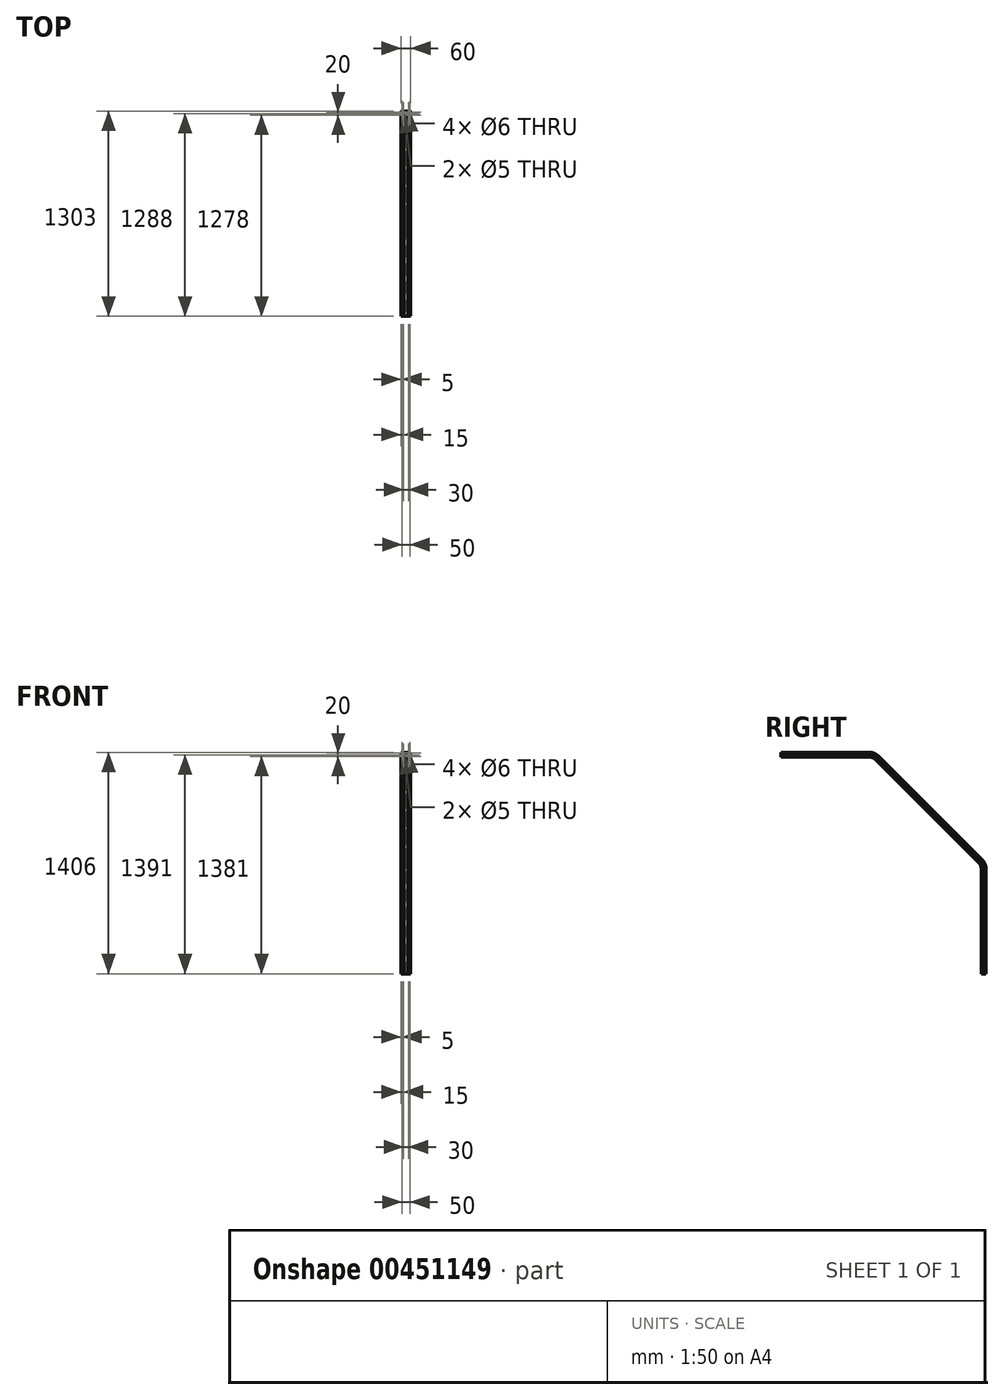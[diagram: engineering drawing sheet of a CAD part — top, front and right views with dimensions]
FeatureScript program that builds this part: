
annotation { "Feature Type Name" : "Feature", "Feature Type Description" : "" }
export const myFeature = defineFeature(function(context is Context, id is Id, definition is map)
    precondition{}
    {
        {
            var Q0;
            Q0=qCreatedBy(makeId("Top.planeOp"),FACE);
            var sketch = newSketch(context, id + "F0", { "sketchPlane" : qUnion([Q0])});
            skLineSegment(sketch, "E0.bottom", {"start": v(30, -15) * mm, "end": v(18.15, -15) * mm});
            skLineSegment(sketch, "E0.top", {"start": v(30, 15) * mm, "end": v(18.15, 15) * mm});
            skLineSegment(sketch, "E0.left", {"start": v(30, -15) * mm, "end": v(30, -3.15) * mm});
            skLineSegment(sketch, "E0.right", {"start": v(-30, -15) * mm, "end": v(-30, -3.15) * mm});
            skPoint(sketch, "E0.middle", {"position": v(0, 0) * mm});
            skLineSegment(sketch, "E1.left", {"start": v(-11.85, 12.5) * mm, "end": v(-11.85, 15) * mm});
            skLineSegment(sketch, "E1.right", {"start": v(-18.15, 12.5) * mm, "end": v(-18.15, 15) * mm});
            skPoint(sketch, "E1.middle", {"position": v(-15, 13.75) * mm});
            skLineSegment(sketch, "E2.bottom", {"start": v(-9.85, 12.5) * mm, "end": v(-11.85, 12.5) * mm});
            skLineSegment(sketch, "E2.left", {"start": v(-9.85, 12.5) * mm, "end": v(-9.85, 6.55) * mm});
            skLineSegment(sketch, "E2.right", {"start": v(-20.15, 12.5) * mm, "end": v(-20.15, 6.55) * mm});
            skPoint(sketch, "E2.middle", {"position": v(-15, 9.52) * mm});
            skArc(sketch, "E3", {"start": v(-20.15, 6.55) * mm, "mid": v(-15, 4.5) * mm, "end": v(-9.85, 6.55) * mm});
            skPoint(sketch, "E4.MirrorP", {"position": v(15, 9.52) * mm});
            skPoint(sketch, "E5.MirrorP", {"position": v(15, 13.75) * mm});
            skLineSegment(sketch, "E6.MirrorCS", {"start": v(11.85, 12.5) * mm, "end": v(11.85, 15) * mm});
            skLineSegment(sketch, "E7.MirrorCS", {"start": v(18.15, 12.5) * mm, "end": v(18.15, 15) * mm});
            skLineSegment(sketch, "E8.MirrorCS", {"start": v(9.85, 12.5) * mm, "end": v(11.85, 12.5) * mm});
            skLineSegment(sketch, "E9.MirrorCS", {"start": v(9.85, 12.5) * mm, "end": v(9.85, 6.55) * mm});
            skArc(sketch, "E10.MirrorCS", {"start": v(20.15, 6.55) * mm, "mid": v(15, 4.5) * mm, "end": v(9.85, 6.55) * mm});
            skLineSegment(sketch, "E11.MirrorCS", {"start": v(20.15, 12.5) * mm, "end": v(20.15, 6.55) * mm});
            skLineSegment(sketch, "E12.trimOffspring", {"start": v(-18.15, 12.5) * mm, "end": v(-20.15, 12.5) * mm});
            skLineSegment(sketch, "E13.trimOffspring", {"start": v(18.15, 12.5) * mm, "end": v(20.15, 12.5) * mm});
            skCircle(sketch, "E14", {"center": v(-15, 0) * mm, "radius": 2.5 * mm});
            skCircle(sketch, "E15", {"center": v(-25, 10) * mm, "radius": 3 * mm});
            skCircle(sketch, "E16.MirrorC", {"center": v(25, 10) * mm, "radius": 3 * mm});
            skCircle(sketch, "E17.MirrorC", {"center": v(25, -10) * mm, "radius": 3 * mm});
            skCircle(sketch, "E18.MirrorC", {"center": v(-25, -10) * mm, "radius": 3 * mm});
            skCircle(sketch, "E19.MirrorC", {"center": v(15, 0) * mm, "radius": 2.5 * mm});
            skLineSegment(sketch, "E20", {"start": v(-7, 12.5) * mm, "end": v(0, 12.5) * mm});
            skLineSegment(sketch, "E21", {"start": v(-7, 12.5) * mm, "end": v(-7, 7) * mm});
            skLineSegment(sketch, "E22", {"start": v(-10, 0) * mm, "end": v(-7, 7) * mm});
            skLineSegment(sketch, "E23.MirrorCS", {"start": v(10, 0) * mm, "end": v(7, 7) * mm});
            skLineSegment(sketch, "E24.MirrorCS", {"start": v(7, 12.5) * mm, "end": v(0, 12.5) * mm});
            skLineSegment(sketch, "E25.MirrorCS", {"start": v(7, 12.5) * mm, "end": v(7, 7) * mm});
            skLineSegment(sketch, "E26.MirrorCS", {"start": v(-18.15, -12.5) * mm, "end": v(-20.15, -12.5) * mm});
            skLineSegment(sketch, "E27.MirrorCS", {"start": v(-9.85, -12.5) * mm, "end": v(-11.85, -12.5) * mm});
            skLineSegment(sketch, "E28.MirrorCS", {"start": v(-9.85, -12.5) * mm, "end": v(-9.85, -6.55) * mm});
            skPoint(sketch, "E29.MirrorP", {"position": v(-15, -13.75) * mm});
            skPoint(sketch, "E30.MirrorP", {"position": v(-15, -9.52) * mm});
            skLineSegment(sketch, "E31.MirrorCS", {"start": v(-18.15, -12.5) * mm, "end": v(-18.15, -15) * mm});
            skLineSegment(sketch, "E32.MirrorCS", {"start": v(-20.15, -12.5) * mm, "end": v(-20.15, -6.55) * mm});
            skLineSegment(sketch, "E33.MirrorCS", {"start": v(-11.85, -12.5) * mm, "end": v(-11.85, -15) * mm});
            skArc(sketch, "E34.MirrorCS", {"start": v(-20.15, -6.55) * mm, "mid": v(-15, -4.5) * mm, "end": v(-9.85, -6.55) * mm});
            skLineSegment(sketch, "E35.MirrorCS", {"start": v(18.15, -12.5) * mm, "end": v(20.15, -12.5) * mm});
            skLineSegment(sketch, "E36.MirrorCS", {"start": v(9.85, -12.5) * mm, "end": v(11.85, -12.5) * mm});
            skPoint(sketch, "E37.MirrorP", {"position": v(15, -13.75) * mm});
            skPoint(sketch, "E38.MirrorP", {"position": v(15, -9.52) * mm});
            skLineSegment(sketch, "E39.MirrorCS", {"start": v(18.15, -12.5) * mm, "end": v(18.15, -15) * mm});
            skArc(sketch, "E40.MirrorCS", {"start": v(20.15, -6.55) * mm, "mid": v(15, -4.5) * mm, "end": v(9.85, -6.55) * mm});
            skLineSegment(sketch, "E41.MirrorCS", {"start": v(9.85, -12.5) * mm, "end": v(9.85, -6.55) * mm});
            skLineSegment(sketch, "E42.MirrorCS", {"start": v(11.85, -12.5) * mm, "end": v(11.85, -15) * mm});
            skLineSegment(sketch, "E43.MirrorCS", {"start": v(20.15, -12.5) * mm, "end": v(20.15, -6.55) * mm});
            skLineSegment(sketch, "E44.MirrorCS", {"start": v(10, 0) * mm, "end": v(7, -7) * mm});
            skLineSegment(sketch, "E45.MirrorCS", {"start": v(7, -12.5) * mm, "end": v(7, -7) * mm});
            skLineSegment(sketch, "E46.MirrorCS", {"start": v(7, -12.5) * mm, "end": v(0, -12.5) * mm});
            skLineSegment(sketch, "E47.MirrorCS", {"start": v(-7, -12.5) * mm, "end": v(0, -12.5) * mm});
            skLineSegment(sketch, "E48.MirrorCS", {"start": v(-10, 0) * mm, "end": v(-7, -7) * mm});
            skLineSegment(sketch, "E49.MirrorCS", {"start": v(-7, -12.5) * mm, "end": v(-7, -7) * mm});
            skLineSegment(sketch, "E50.left", {"start": v(-27.5, 3.15) * mm, "end": v(-30, 3.15) * mm});
            skLineSegment(sketch, "E50.right", {"start": v(-27.5, -3.15) * mm, "end": v(-30, -3.15) * mm});
            skLineSegment(sketch, "E51.bottom", {"start": v(-27.5, 5.15) * mm, "end": v(-27.5, 3.15) * mm});
            skLineSegment(sketch, "E51.left", {"start": v(-27.5, 5.15) * mm, "end": v(-21.55, 5.15) * mm});
            skLineSegment(sketch, "E51.right", {"start": v(-27.5, -5.15) * mm, "end": v(-21.55, -5.15) * mm});
            skArc(sketch, "E52", {"start": v(-21.55, -5.15) * mm, "mid": v(-19.5, 0) * mm, "end": v(-21.55, 5.15) * mm});
            skLineSegment(sketch, "E53.trimOffspring", {"start": v(-27.5, -3.15) * mm, "end": v(-27.5, -5.15) * mm});
            skArc(sketch, "E54.MirrorCS", {"start": v(21.55, -5.15) * mm, "mid": v(19.5, 0) * mm, "end": v(21.55, 5.15) * mm});
            skLineSegment(sketch, "E55.MirrorCS", {"start": v(27.5, -5.15) * mm, "end": v(21.55, -5.15) * mm});
            skLineSegment(sketch, "E56.MirrorCS", {"start": v(27.5, -3.15) * mm, "end": v(30, -3.15) * mm});
            skLineSegment(sketch, "E57.MirrorCS", {"start": v(27.5, 5.15) * mm, "end": v(27.5, 3.15) * mm});
            skLineSegment(sketch, "E58.MirrorCS", {"start": v(27.5, 3.15) * mm, "end": v(30, 3.15) * mm});
            skLineSegment(sketch, "E59.MirrorCS", {"start": v(27.5, 5.15) * mm, "end": v(21.55, 5.15) * mm});
            skLineSegment(sketch, "E60.MirrorCS", {"start": v(27.5, -3.15) * mm, "end": v(27.5, -5.15) * mm});
            skLineSegment(sketch, "E61.trimOffspring", {"start": v(30, 3.15) * mm, "end": v(30, 15) * mm});
            skLineSegment(sketch, "E62.trimOffspring", {"start": v(11.85, -15) * mm, "end": v(-11.85, -15) * mm});
            skLineSegment(sketch, "E63.trimOffspring", {"start": v(11.85, 15) * mm, "end": v(-11.85, 15) * mm});
            skLineSegment(sketch, "E64.trimOffspring", {"start": v(-18.15, -15) * mm, "end": v(-30, -15) * mm});
            skLineSegment(sketch, "E65.trimOffspring", {"start": v(-30, 3.15) * mm, "end": v(-30, 15) * mm});
            skLineSegment(sketch, "E66.trimOffspring", {"start": v(-18.15, 15) * mm, "end": v(-30, 15) * mm});
            skSolve(sketch);
        }
        {
            var Q0;
            Q0=qCreatedBy(makeId("Right.planeOp"),FACE);
            var sketch = newSketch(context, id + "F1", { "sketchPlane" : qUnion([Q0])});
            skLineSegment(sketch, "E67", {"start": v(-15, 0) * mm, "end": v(-15, 667.29) * mm});
            skLineSegment(sketch, "E68", {"start": v(-29.64, 702.64) * mm, "end": v(-688.36, 1361.36) * mm});
            skPoint(sketch, "E69.visualSharp", {"position": v(-15, 688) * mm});
            skArc(sketch, "E69.filletArc", {"start": v(-15, 667.29) * mm, "mid": v(-18.8, 686.42) * mm, "end": v(-29.64, 702.64) * mm});
            skLineSegment(sketch, "E70", {"start": v(-723.71, 1376) * mm, "end": v(-1288, 1376) * mm});
            skPoint(sketch, "E71.visualSharp", {"position": v(-703, 1376) * mm});
            skArc(sketch, "E71.filletArc", {"start": v(-688.36, 1361.36) * mm, "mid": v(-704.58, 1372.2) * mm, "end": v(-723.71, 1376) * mm});
            skSolve(sketch);
        }
        {
            var Q0;
            Q0 = qSketchRegion(id + "F0", true);
            var Q1;
            Q1 = qConstructionFilter(qBodyType(qCreatedBy(id + "F1" ,EDGE), BodyType.WIRE), ConstructionObject.NO);
            sweep(context, id + "F2", {"profiles" : qUnion([Q0]), "path" : qUnion([Q1])});
        }
    });
